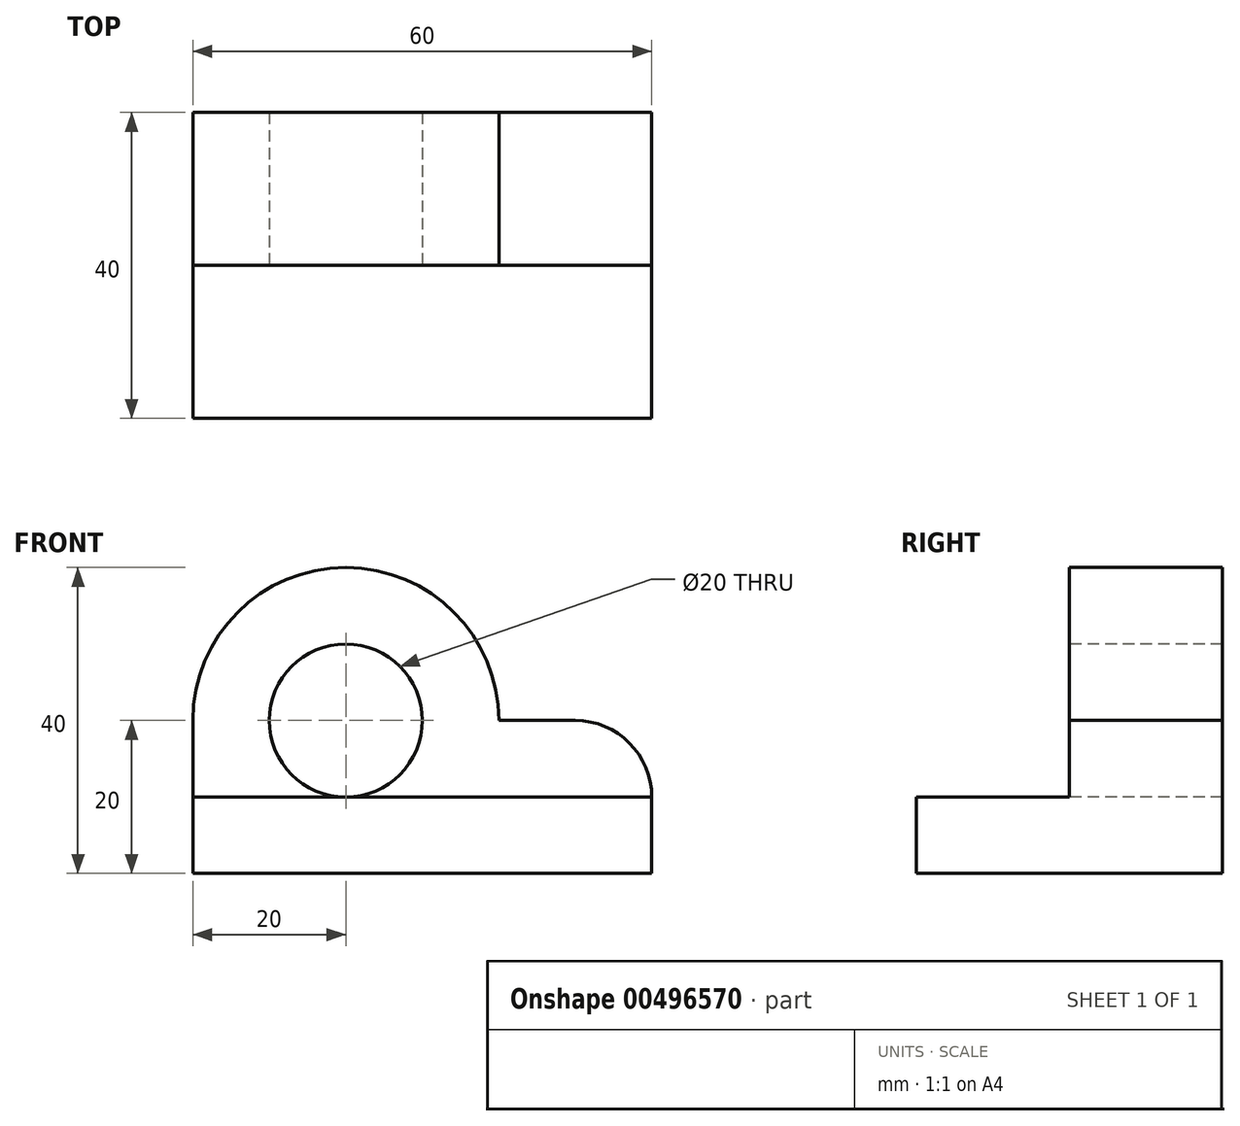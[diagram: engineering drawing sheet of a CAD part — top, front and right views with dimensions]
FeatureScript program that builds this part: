
annotation { "Feature Type Name" : "Feature", "Feature Type Description" : "" }
export const myFeature = defineFeature(function(context is Context, id is Id, definition is map)
    precondition{}
    {
        {
            var Q0;
            Q0=qCreatedBy(makeId("Top.planeOp"),FACE);
            var sketch = newSketch(context, id + "F0", { "sketchPlane" : qUnion([Q0])});
            skLineSegment(sketch, "E0.bottom", {"start": v(0, 0) * mm, "end": v(60, 0) * mm});
            skLineSegment(sketch, "E0.top", {"start": v(0, 40) * mm, "end": v(60, 40) * mm});
            skLineSegment(sketch, "E0.left", {"start": v(0, 0) * mm, "end": v(0, 40) * mm});
            skLineSegment(sketch, "E0.right", {"start": v(60, 0) * mm, "end": v(60, 40) * mm});
            skSolve(sketch);
        }
        {
            var Q0;
            Q0 = qSketchRegion(id + "F0", true);
            extrude(context, id + "F1", {"entities" : qUnion([Q0]), "depth" : 10 * mm});
        }
        {
            var Q0;
            Q0=qCreatedBy(makeId("Front.planeOp"),FACE);
            var sketch = newSketch(context, id + "F2", { "sketchPlane" : qUnion([Q0])});
            skPoint(sketch, "E1", {"position": v(20, 20) * mm});
            skArc(sketch, "E2", {"start": v(40, 20) * mm, "mid": v(20, 40) * mm, "end": v(0, 20) * mm});
            skLineSegment(sketch, "E3", {"start": v(0, 20) * mm, "end": v(0, 10) * mm});
            skLineSegment(sketch, "E4", {"start": v(40, 20) * mm, "end": v(50, 20) * mm});
            skLineSegment(sketch, "E5", {"start": v(60, 10) * mm, "end": v(60, 10) * mm});
            skPoint(sketch, "E6.visualSharp", {"position": v(60, 20) * mm});
            skArc(sketch, "E6.filletArc", {"start": v(60, 10) * mm, "mid": v(57.07, 17.07) * mm, "end": v(50, 20) * mm});
            skLineSegment(sketch, "E7", {"start": v(0, 10) * mm, "end": v(60, 10) * mm});
            skSolve(sketch);
        }
        {
            var Q0;
            Q0 = qSketchRegion(id + "F2", true);
            extrude(context, id + "F3", {"entities" : qUnion([Q0]), "operationType" : NewBodyOperationType.ADD, "oppositeDirection" : true, "depth" : 40 * mm, "hasSecondDirection" : true, "secondDirectionOppositeDirection" : true, "secondDirectionDepth" : 20 * mm});
        }
        {
            var Q0;
            Q0=makeQuery(id+"F3.opExtrude","CAP_FACE",FACE,{"disambiguationData":[OSD([sQuery(id+"F2.wireOp",EDGE,"E2"),sQuery(id+"F2.wireOp",EDGE,"E3"),sQuery(id+"F2.wireOp",EDGE,"E4"),sQuery(id+"F2.wireOp",EDGE,"E6.filletArc"),sQuery(id+"F2.wireOp",EDGE,"E7")])],"isStart":true});
            var sketch = newSketch(context, id + "F4", { "sketchPlane" : qUnion([Q0])});
            skCircle(sketch, "E8", {"center": v(20, 20) * mm, "radius": 10 * mm});
            skSolve(sketch);
        }
        {
            var Q0;
            Q0 = qSketchRegion(id + "F4", true);
            extrude(context, id + "F5", {"entities" : qUnion([Q0]), "operationType" : NewBodyOperationType.REMOVE, "oppositeDirection" : true, "depth" : 25 * mm});
        }
    });
